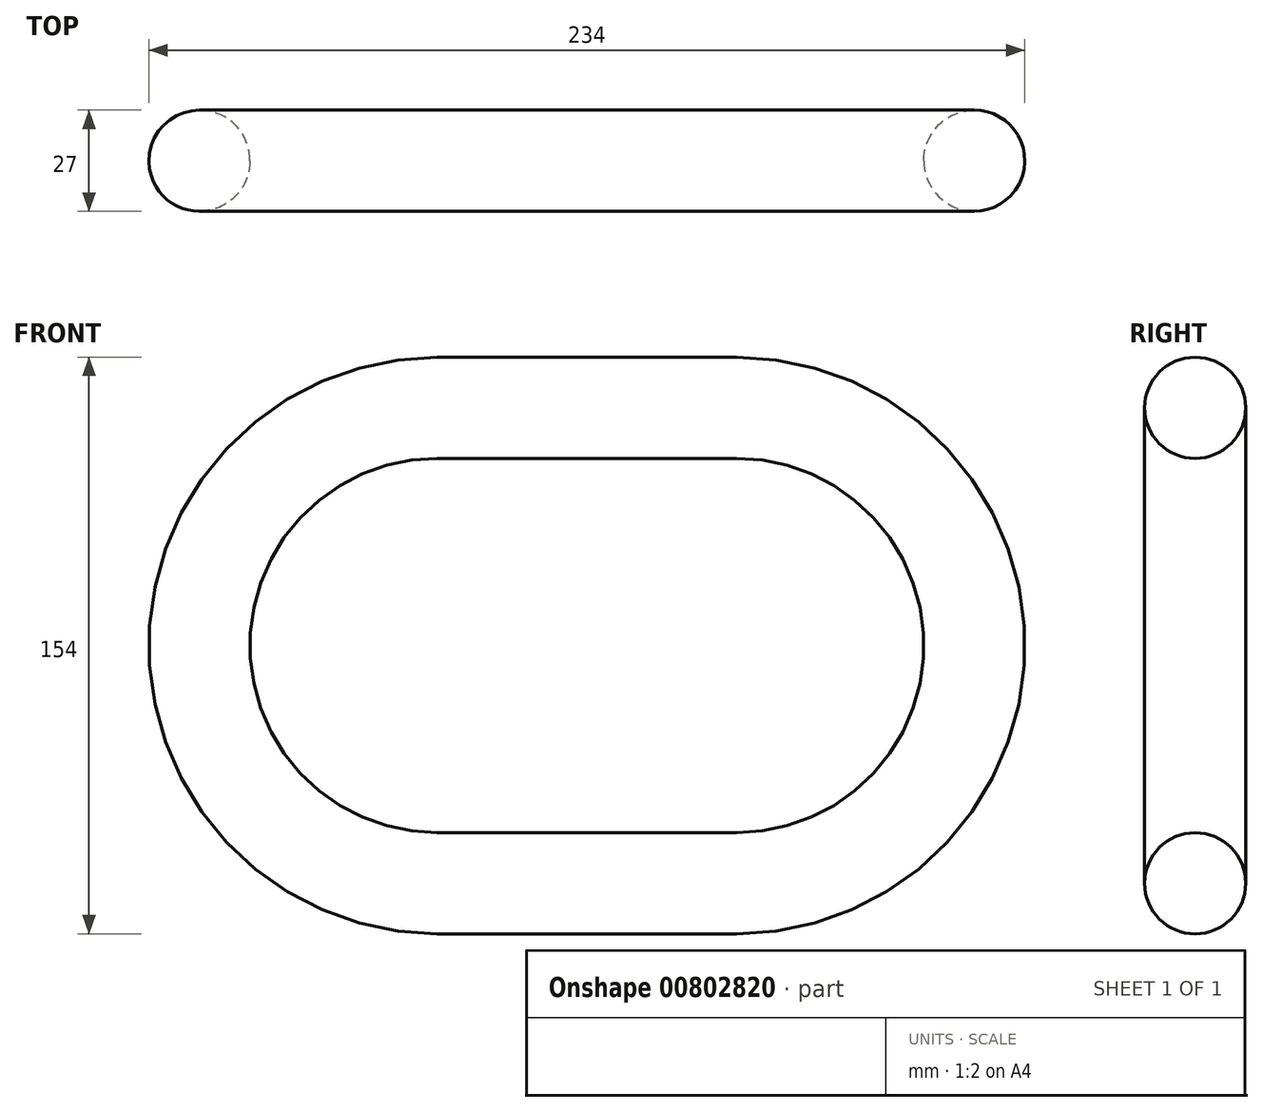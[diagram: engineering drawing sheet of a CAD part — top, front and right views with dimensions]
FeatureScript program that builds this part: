
annotation { "Feature Type Name" : "Feature", "Feature Type Description" : "" }
export const myFeature = defineFeature(function(context is Context, id is Id, definition is map)
    precondition{}
    {
        {
            var Q0;
            Q0=qCreatedBy(makeId("Front.planeOp"),FACE);
            var sketch = newSketch(context, id + "F0", { "sketchPlane" : qUnion([Q0])});
            skLineSegment(sketch, "E0.bottom", {"start": v(40, -50) * mm, "end": v(-40, -50) * mm});
            skLineSegment(sketch, "E0.top", {"start": v(40, 50) * mm, "end": v(-40, 50) * mm});
            skLineSegment(sketch, "E0.left", {"start": v(90, 0) * mm, "end": v(90, 0) * mm});
            skLineSegment(sketch, "E0.right", {"start": v(-90, 0) * mm, "end": v(-90, 0) * mm});
            skPoint(sketch, "E0.middle", {"position": v(0, 0) * mm});
            skPoint(sketch, "E1.visualSharp", {"position": v(90, 50) * mm});
            skArc(sketch, "E1.filletArc", {"start": v(90, 0) * mm, "mid": v(75.36, 35.36) * mm, "end": v(40, 50) * mm});
            skPoint(sketch, "E2.visualSharp", {"position": v(90, -50) * mm});
            skArc(sketch, "E2.filletArc", {"start": v(40, -50) * mm, "mid": v(75.36, -35.36) * mm, "end": v(90, 0) * mm});
            skPoint(sketch, "E3.visualSharp", {"position": v(-90, -50) * mm});
            skArc(sketch, "E3.filletArc", {"start": v(-90, 0) * mm, "mid": v(-75.36, -35.36) * mm, "end": v(-40, -50) * mm});
            skPoint(sketch, "E4.visualSharp", {"position": v(-90, 50) * mm});
            skArc(sketch, "E4.filletArc", {"start": v(-40, 50) * mm, "mid": v(-75.36, 35.36) * mm, "end": v(-90, 0) * mm});
            skSolve(sketch);
        }
        {
            var Q0;
            Q0=qCreatedBy(makeId("Right.planeOp"),FACE);
            var sketch = newSketch(context, id + "F1", { "sketchPlane" : qUnion([Q0])});
            skCircle(sketch, "E5", {"center": v(0, 63.5) * mm, "radius": 13.5 * mm});
            skSolve(sketch);
        }
        {
            var Q0;
            Q0=makeQuery(id+"F1.imprint","IMPRINT",FACE,{"disambiguationData":[TD([[makeQuery(id+"F1.imprint","IMPRINT",EDGE,{"derivedFrom":sQuery(id+"F1.wireOp",EDGE,"E5")}),1.0]])]});
            var Q1;
            Q1=sQuery(id+"F0.wireOp",EDGE,"E0.top");
            var Q2;
            Q2=sQuery(id+"F0.wireOp",EDGE,"E1.filletArc");
            var Q3;
            Q3=sQuery(id+"F0.wireOp",EDGE,"E2.filletArc");
            var Q4;
            Q4=sQuery(id+"F0.wireOp",EDGE,"E0.bottom");
            var Q5;
            Q5=sQuery(id+"F0.wireOp",EDGE,"E3.filletArc");
            var Q6;
            Q6=sQuery(id+"F0.wireOp",EDGE,"E4.filletArc");
            sweep(context, id + "F2", {"profiles" : qUnion([Q0]), "path" : qUnion([Q1, Q2, Q3, Q4, Q5, Q6])});
        }
    });
